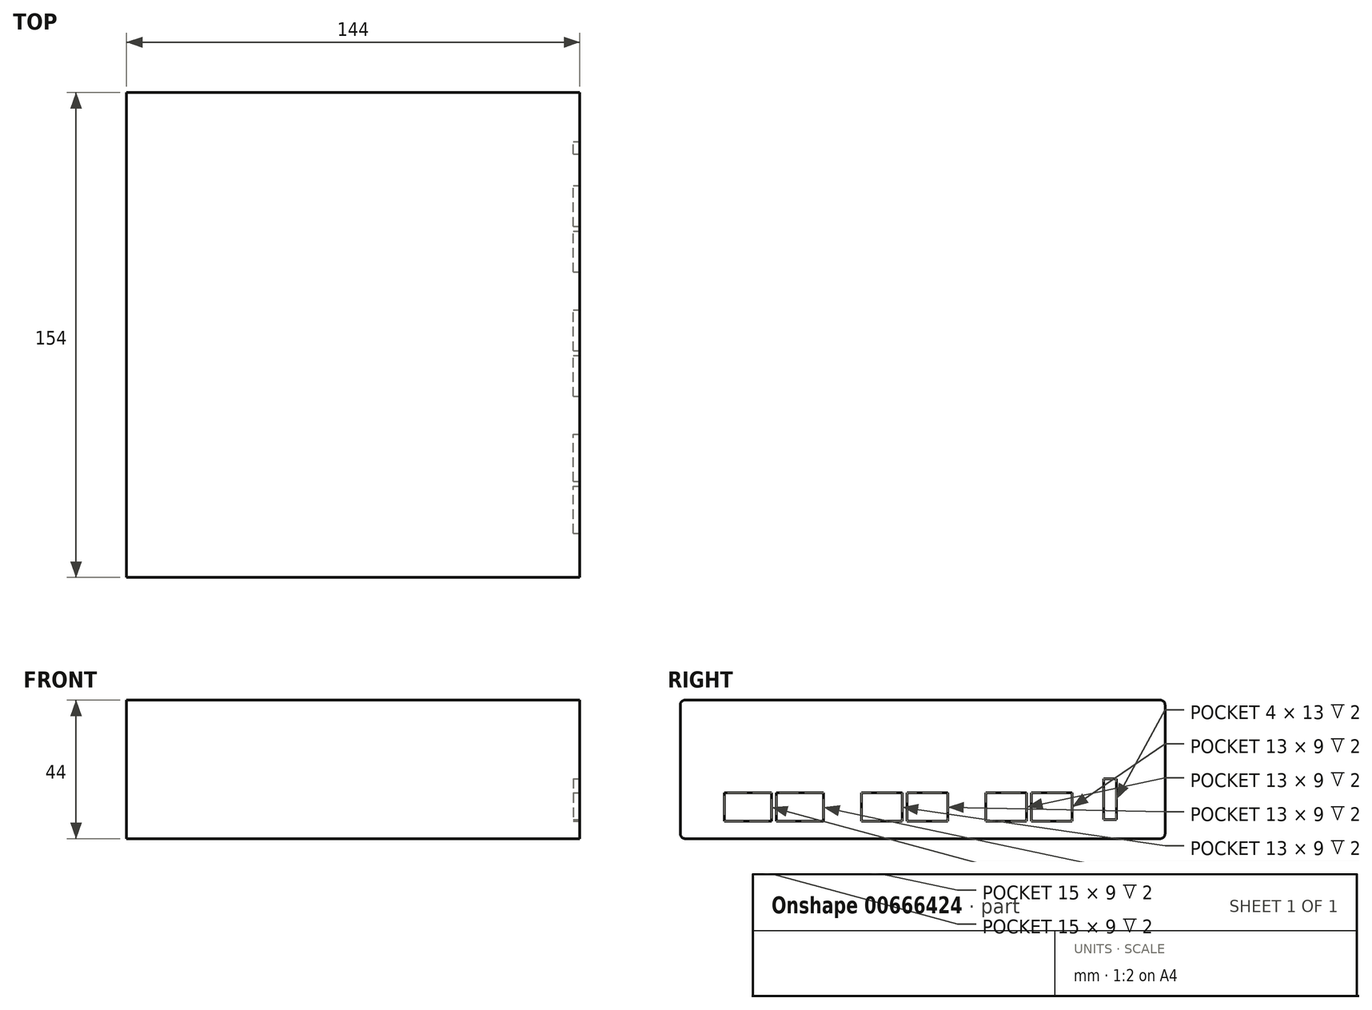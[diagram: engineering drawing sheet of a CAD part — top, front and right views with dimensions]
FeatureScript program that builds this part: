
annotation { "Feature Type Name" : "Feature", "Feature Type Description" : "" }
export const myFeature = defineFeature(function(context is Context, id is Id, definition is map)
    precondition{}
    {
        {
            var Q0;
            Q0=qCreatedBy(makeId("Top.planeOp"),FACE);
            var sketch = newSketch(context, id + "F0", { "sketchPlane" : qUnion([Q0])});
            skLineSegment(sketch, "E0.bottom", {"start": v(-72, -77) * mm, "end": v(72, -77) * mm});
            skLineSegment(sketch, "E0.top", {"start": v(-72, 77) * mm, "end": v(72, 77) * mm});
            skLineSegment(sketch, "E0.left", {"start": v(-72, -77) * mm, "end": v(-72, 77) * mm});
            skLineSegment(sketch, "E0.right", {"start": v(72, -77) * mm, "end": v(72, 77) * mm});
            skPoint(sketch, "E0.middle", {"position": v(0, 0) * mm});
            skSolve(sketch);
        }
        {
            var Q0;
            Q0=makeQuery(id+"F0.imprint","IMPRINT",FACE,{"disambiguationData":[TD([[makeQuery(id+"F0.imprint","IMPRINT",EDGE,{"derivedFrom":sQuery(id+"F0.wireOp",EDGE,"E0.bottom")}),1.0]])]});
            extrude(context, id + "F1", {"entities" : qUnion([Q0]), "depth" : 44 * mm, "offsetDistance" : 25 * mm});
        }
        {
            var Q0;
            Q0=makeQuery(id+"F1.opExtrude","SWEPT_FACE",FACE,{"disambiguationData":[OSD([sQuery(id+"F0.wireOp",EDGE,"E0.right")])]});
            var sketch = newSketch(context, id + "F2", { "sketchPlane" : qUnion([Q0])});
            skLineSegment(sketch, "E1.bottom", {"start": v(-63, 5.5) * mm, "end": v(-48, 5.5) * mm});
            skLineSegment(sketch, "E1.top", {"start": v(-63, 14.5) * mm, "end": v(-48, 14.5) * mm});
            skLineSegment(sketch, "E1.left", {"start": v(-63, 5.5) * mm, "end": v(-63, 14.5) * mm});
            skLineSegment(sketch, "E1.right", {"start": v(-48, 5.5) * mm, "end": v(-48, 14.5) * mm});
            skLineSegment(sketch, "E2.bottom", {"start": v(-46.5, 14.5) * mm, "end": v(-31.5, 14.5) * mm});
            skLineSegment(sketch, "E2.top", {"start": v(-46.5, 5.5) * mm, "end": v(-31.5, 5.5) * mm});
            skLineSegment(sketch, "E2.left", {"start": v(-46.5, 14.5) * mm, "end": v(-46.5, 5.5) * mm});
            skLineSegment(sketch, "E2.right", {"start": v(-31.5, 14.5) * mm, "end": v(-31.5, 5.5) * mm});
            skLineSegment(sketch, "E3.bottom", {"start": v(57.5, 19) * mm, "end": v(61.5, 19) * mm});
            skLineSegment(sketch, "E3.top", {"start": v(57.5, 6) * mm, "end": v(61.5, 6) * mm});
            skLineSegment(sketch, "E3.left", {"start": v(57.5, 19) * mm, "end": v(57.5, 6) * mm});
            skLineSegment(sketch, "E3.right", {"start": v(61.5, 19) * mm, "end": v(61.5, 6) * mm});
            skLineSegment(sketch, "E4.bottom", {"start": v(-19.5, 5.5) * mm, "end": v(-6.5, 5.5) * mm});
            skLineSegment(sketch, "E4.top", {"start": v(-19.5, 14.5) * mm, "end": v(-6.5, 14.5) * mm});
            skLineSegment(sketch, "E4.left", {"start": v(-19.5, 5.5) * mm, "end": v(-19.5, 14.5) * mm});
            skLineSegment(sketch, "E4.right", {"start": v(-6.5, 5.5) * mm, "end": v(-6.5, 14.5) * mm});
            skLineSegment(sketch, "E5.bottom", {"start": v(-5, 14.5) * mm, "end": v(8, 14.5) * mm});
            skLineSegment(sketch, "E5.top", {"start": v(-5, 5.5) * mm, "end": v(8, 5.5) * mm});
            skLineSegment(sketch, "E5.left", {"start": v(-5, 14.5) * mm, "end": v(-5, 5.5) * mm});
            skLineSegment(sketch, "E5.right", {"start": v(8, 14.5) * mm, "end": v(8, 5.5) * mm});
            skLineSegment(sketch, "E6.bottom", {"start": v(20, 5.5) * mm, "end": v(33, 5.5) * mm});
            skLineSegment(sketch, "E6.top", {"start": v(20, 14.5) * mm, "end": v(33, 14.5) * mm});
            skLineSegment(sketch, "E6.left", {"start": v(20, 5.5) * mm, "end": v(20, 14.5) * mm});
            skLineSegment(sketch, "E6.right", {"start": v(33, 5.5) * mm, "end": v(33, 14.5) * mm});
            skLineSegment(sketch, "E7.bottom", {"start": v(34.5, 14.5) * mm, "end": v(47.5, 14.5) * mm});
            skLineSegment(sketch, "E7.top", {"start": v(34.5, 5.5) * mm, "end": v(47.5, 5.5) * mm});
            skLineSegment(sketch, "E7.left", {"start": v(34.5, 14.5) * mm, "end": v(34.5, 5.5) * mm});
            skLineSegment(sketch, "E7.right", {"start": v(47.5, 14.5) * mm, "end": v(47.5, 5.5) * mm});
            skSolve(sketch);
        }
        {
            var Q0;
            Q0=makeQuery(id+"F2.imprint","IMPRINT",FACE,{"disambiguationData":[TD([[makeQuery(id+"F2.imprint","IMPRINT",EDGE,{"derivedFrom":sQuery(id+"F2.wireOp",EDGE,"E1.bottom")}),1.0]])]});
            var Q1;
            Q1=makeQuery(id+"F2.imprint","IMPRINT",FACE,{"disambiguationData":[TD([[makeQuery(id+"F2.imprint","IMPRINT",EDGE,{"derivedFrom":sQuery(id+"F2.wireOp",EDGE,"E2.bottom")}),-1.0]])]});
            var Q2;
            Q2=makeQuery(id+"F2.imprint","IMPRINT",FACE,{"disambiguationData":[TD([[makeQuery(id+"F2.imprint","IMPRINT",EDGE,{"derivedFrom":sQuery(id+"F2.wireOp",EDGE,"E4.bottom")}),1.0]])]});
            var Q3;
            Q3=makeQuery(id+"F2.imprint","IMPRINT",FACE,{"disambiguationData":[TD([[makeQuery(id+"F2.imprint","IMPRINT",EDGE,{"derivedFrom":sQuery(id+"F2.wireOp",EDGE,"E5.bottom")}),-1.0]])]});
            var Q4;
            Q4=makeQuery(id+"F2.imprint","IMPRINT",FACE,{"disambiguationData":[TD([[makeQuery(id+"F2.imprint","IMPRINT",EDGE,{"derivedFrom":sQuery(id+"F2.wireOp",EDGE,"E6.bottom")}),1.0]])]});
            var Q5;
            Q5=makeQuery(id+"F2.imprint","IMPRINT",FACE,{"disambiguationData":[TD([[makeQuery(id+"F2.imprint","IMPRINT",EDGE,{"derivedFrom":sQuery(id+"F2.wireOp",EDGE,"E7.bottom")}),-1.0]])]});
            var Q6;
            Q6=makeQuery(id+"F2.imprint","IMPRINT",FACE,{"disambiguationData":[TD([[makeQuery(id+"F2.imprint","IMPRINT",EDGE,{"derivedFrom":sQuery(id+"F2.wireOp",EDGE,"E3.bottom")}),-1.0]])]});
            extrude(context, id + "F3", {"entities" : qUnion([Q0, Q1, Q2, Q3, Q4, Q5, Q6]), "operationType" : NewBodyOperationType.REMOVE, "oppositeDirection" : true, "depth" : 2 * mm, "offsetDistance" : 25 * mm});
        }
        {
            var Q0;
            Q0=makeQuery(id+"F1.opExtrude","CAP_EDGE",EDGE,{"disambiguationData":[OSD([sQuery(id+"F0.wireOp",EDGE,"E0.bottom")])],"isStart":false});
            var Q1;
            Q1=makeQuery(id+"F1.opExtrude","CAP_EDGE",EDGE,{"disambiguationData":[OSD([sQuery(id+"F0.wireOp",EDGE,"E0.top")])],"isStart":false});
            var Q2;
            Q2=makeQuery(id+"F1.opExtrude","CAP_EDGE",EDGE,{"disambiguationData":[OSD([sQuery(id+"F0.wireOp",EDGE,"E0.bottom")])],"isStart":true});
            var Q3;
            Q3=makeQuery(id+"F1.opExtrude","CAP_EDGE",EDGE,{"disambiguationData":[OSD([sQuery(id+"F0.wireOp",EDGE,"E0.top")])],"isStart":true});
            fillet(context, id + "F4", {"entities" : qUnion([Q0, Q1, Q2, Q3]), "radius" : 1.5 * mm, "tangentPropagation" : true, "allowEdgeOverflow" : false});
        }
    });
